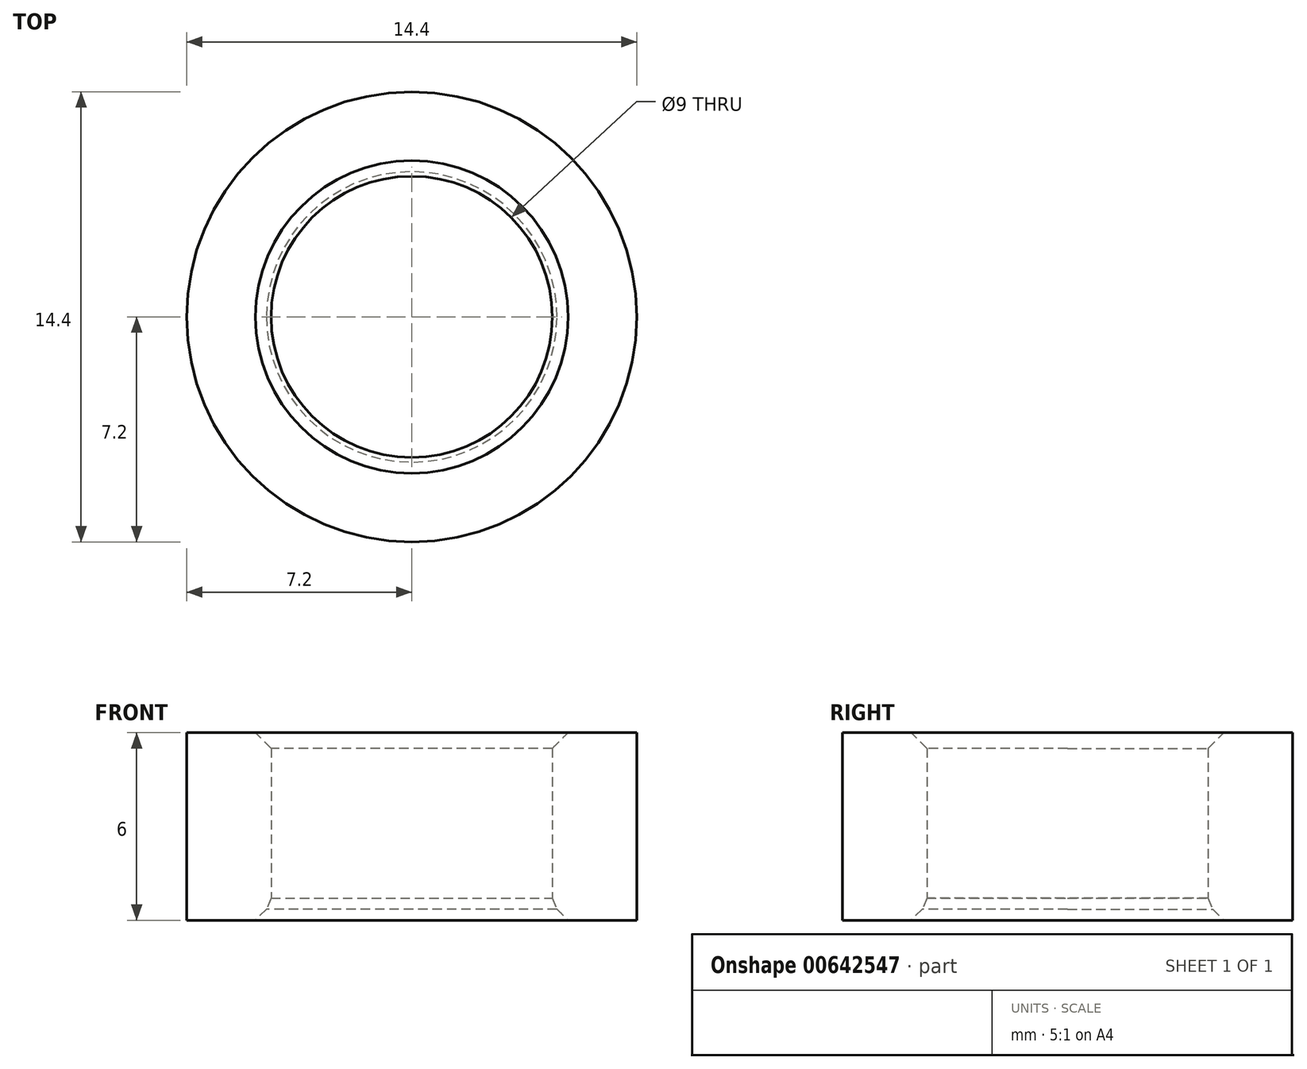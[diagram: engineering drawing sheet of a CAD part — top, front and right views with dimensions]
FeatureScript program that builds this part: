
annotation { "Feature Type Name" : "Feature", "Feature Type Description" : "" }
export const myFeature = defineFeature(function(context is Context, id is Id, definition is map)
    precondition{}
    {
        {
            var Q0;
            Q0=qCreatedBy(makeId("Top.planeOp"),FACE);
            var sketch = newSketch(context, id + "F0", { "sketchPlane" : qUnion([Q0])});
            skCircle(sketch, "E0", {"center": v(0, 0) * mm, "radius": 7.2 * mm});
            skCircle(sketch, "E1", {"center": v(0, 0) * mm, "radius": 4.5 * mm});
            skCircle(sketch, "E2", {"center": v(0, 0) * mm, "radius": 3.5 * mm});
            skSolve(sketch);
        }
        {
            var Q0;
            Q0 = qSketchRegion(id + "F0", true);
            extrude(context, id + "F1", {"entities" : qUnion([Q0]), "depth" : 6 * mm, "offsetDistance" : 25.4 * mm});
        }
        {
            var Q0;
            Q0=makeQuery(id+"F1.opExtrude","CAP_EDGE",EDGE,{"disambiguationData":[OSD([sQuery(id+"F0.wireOp",EDGE,"E1")])],"isStart":true});
            chamfer(context, id + "F2", {"entities" : qUnion([Q0]), "chamferType" : ChamferType.OFFSET_ANGLE, "width" : 0.5 * mm, "oppositeDirection" : false, "angle" : 45 * degree, "tangentPropagation" : true});
        }
        {
            var Q0;
            Q0=makeQuery(id+"F1.opExtrude","SWEPT_FACE",FACE,{"disambiguationData":[OSD([sQuery(id+"F0.wireOp",EDGE,"E1")])]});
            chamfer(context, id + "F3", {"entities" : qUnion([Q0]), "width" : 0.5 * mm, "tangentPropagation" : true});
        }
    });
